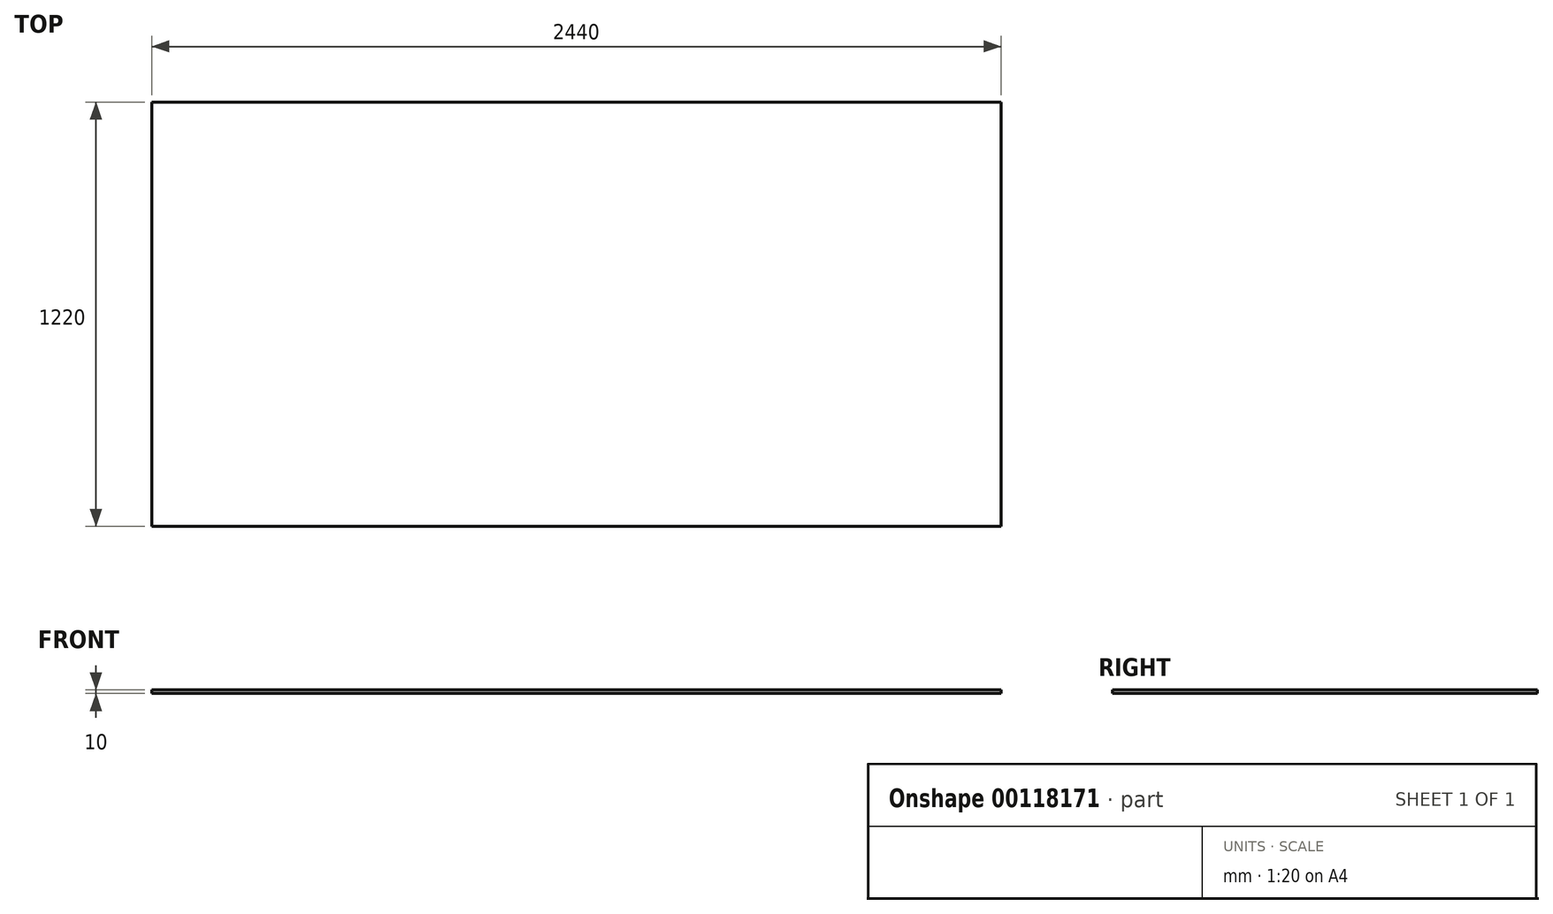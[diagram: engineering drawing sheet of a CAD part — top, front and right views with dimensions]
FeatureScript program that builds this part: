
annotation { "Feature Type Name" : "Feature", "Feature Type Description" : "" }
export const myFeature = defineFeature(function(context is Context, id is Id, definition is map)
    precondition{}
    {
        {
            var Q0;
            Q0=qCreatedBy(makeId("Top.planeOp"),FACE);
            var sketch = newSketch(context, id + "F0", { "sketchPlane" : qUnion([Q0])});
            skLineSegment(sketch, "E0.bottom", {"start": v(0, 0) * mm, "end": v(2440, 0) * mm});
            skLineSegment(sketch, "E0.top", {"start": v(0, -1220) * mm, "end": v(2440, -1220) * mm});
            skLineSegment(sketch, "E0.left", {"start": v(0, 0) * mm, "end": v(0, -1220) * mm});
            skLineSegment(sketch, "E0.right", {"start": v(2440, 0) * mm, "end": v(2440, -1220) * mm});
            skSolve(sketch);
        }
        {
            var Q0;
            Q0=makeQuery(id+"F0.imprint","IMPRINT",FACE,{"disambiguationData":[TD([[makeQuery(id+"F0.imprint","IMPRINT",EDGE,{"derivedFrom":sQuery(id+"F0.wireOp",EDGE,"E0.bottom")}),-1.0]])]});
            extrude(context, id + "F1", {"entities" : qUnion([Q0]), "depth" : 10 * mm});
        }
    });
